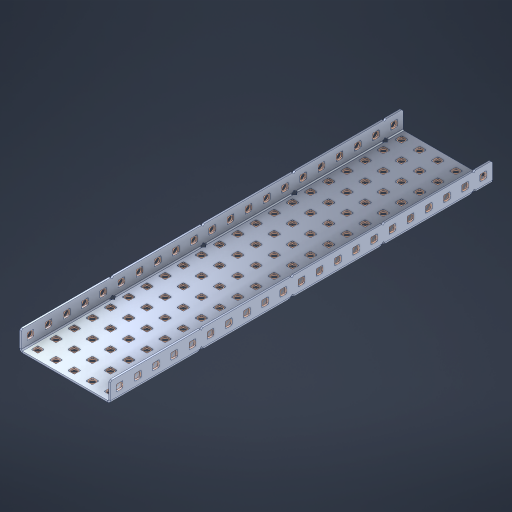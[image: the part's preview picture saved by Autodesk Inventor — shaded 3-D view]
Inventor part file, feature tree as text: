
AUTODESK INVENTOR PART (.ipt)
format: ipt  version: 2023 (Build 270158000, 158)  size: 1,724,416 bytes
history: native  units: in
note: dims shown in document units (in); Inventor stores cm internally (conversion verified against a paired STEP export)
features: other x152, extrude x146, sheet_metal_op x10, sketch x8, mirror x1, pattern_linear x1, chamfer x1
ambient origin geometry x8: Origin, YZ Plane, XZ Plane, XY Plane, X Axis, Y Axis, Z Axis, Center Point
bodies: Solid1 (feature_tree), Body (feature_tree)
feature tree (319):
  other  "Flange Pattern Plane"
  sheet_metal_op  "Flange Pattern"
  sheet_metal_op  "Body Pattern"
  other  "Arc Length"
  mirror  "Notch Mirror"
  pattern_linear  "Notch Pattern"  Spacing1=0.1875in  [1 undecoded]
  chamfer  "End Chamfer"
  extrude  "Half Cut"  Depth=0.0469in
  sketch  "Sketch1"  dims[d0=2.5in]
  other  "Plate1"
  sketch  "Sketch2"  dims[d1=10.5in]
  other  "Plate2"
  sheet_metal_op  "Bend1"
  sheet_metal_op  "Corner1"
  sketch  "Sketch3"  dims[d2=0.0469in]
  other  "Flange Pattern Sketch"
  sketch  "Sketch7"  dims[d3=0.0469in]
  other  "Srf1"
  other  "Srf2"
  sketch  "Sketch8"  dims[d4=0.0234in]
  sketch  "Sketch9"  dims[d5=0.0938in]
  other  "Srf91"
  sheet_metal_op  "Body Pattern Sketch"
  other  "Srf92"
  sketch  "Sketch13"  dims[d6=0.0469in]
  sketch  "Sketch14"  dims[d7=0.5in d8=90.0deg d9=0.0312in d10=0.1875in d11=0.0469in d12=0.0469in d16=0.182in d17=0.02in d18=0.0469in d19=0.0in d20=0.25in d21=0.25in d46=0.172in d47=1.0in d48=0.0in d49=0.182in d50=0.02in d51=0.25in d52=0.25in d53=0.0469in d54=0.0in d55=0.172in d56=1.0in d57=0.0in d60=8.2677in d62=0.5in d63=1.9685in d65=0.5in d85=0.1227in d86=0.1659in d88=0.04in d89=0.0469in d90=0.0in d91=0.04in d92=0.0491in d95=2.5in d96=0.04in d97=0.25in d98=45.0deg d101=0.0in d102=2.497in d131=2.5in d132=8.2677in d134=0.5in d139=0.5in]
  other  "Srf856"
  other  "Srf1310"
  other  "Srf1311"
  other  "Srf1312"
  other  "Srf1376"
  other  "Srf1377"
  other  "Srf1728"
  other  "Srf1755"
  other  "Srf1878"
  other  "Srf1879"
  other  "Srf1880"
  other  "Srf1881"
  other  "Srf1882"
  other  "Srf1883"
  other  "Srf1884"
  other  "Srf1885"
  other  "Srf1886"
  other  "Srf1887"
  other  "Srf1888"
  other  "Srf1889"
  other  "Srf1890"
  other  "Srf1891"
  other  "Srf1892"
  other  "Srf1893"
  other  "Srf1894"
  other  "Srf1895"
  other  "Srf1896"
  other  "Srf1897"
  other  "Srf1898"
  other  "Srf1899"
  other  "Srf1900"
  other  "Srf1901"
  other  "Srf1902"
  other  "Srf1903"
  other  "Srf1904"
  other  "Srf1905"
  other  "Srf1906"
  other  "Srf1942"
  other  "Srf1943"
  other  "Srf1944"
  other  "Srf1945"
  other  "Srf1946"
  other  "Srf1947"
  other  "Srf1948"
  other  "Srf1949"
  other  "Srf1950"
  other  "Srf1951"
  other  "Srf1952"
  other  "Srf1953"
  other  "Srf1954"
  other  "Srf1955"
  other  "Srf1956"
  other  "Srf1957"
  other  "Srf1958"
  other  "Srf1959"
  other  "Srf1960"
  other  "Srf1961"
  other  "Srf1962"
  other  "Srf1963"
  other  "Srf1964"
  other  "Srf1965"
  other  "Srf1966"
  other  "Srf1967"
  other  "Srf1968"
  other  "Srf1969"
  other  "Srf1970"
  other  "Srf2111"
  other  "Srf2112"
  other  "Srf2113"
  other  "Srf2114"
  other  "Srf2115"
  other  "Srf2116"
  other  "Srf2117"
  other  "Srf2146"
  other  "Srf2147"
  other  "Srf2148"
  other  "Srf2149"
  other  "Srf2150"
  other  "Srf2151"
  other  "Srf2152"
  other  "Srf2153"
  other  "Srf2154"
  other  "Srf2155"
  other  "Srf2156"
  other  "Srf2157"
  other  "Srf2158"
  other  "Srf2159"
  other  "Srf2160"
  other  "Srf2161"
  other  "Srf2162"
  other  "Srf2163"
  other  "Srf2164"
  other  "Srf2165"
  other  "Srf2166"
  other  "Srf2167"
  other  "Srf2168"
  other  "Srf2169"
  other  "Srf2170"
  other  "Srf2171"
  other  "Srf2172"
  other  "Srf2173"
  other  "Srf2174"
  other  "Srf2175"
  other  "Srf2176"
  other  "Srf2177"
  other  "Srf2178"
  other  "Srf2179"
  other  "Srf2180"
  other  "Srf2181"
  other  "Srf2182"
  other  "Srf2183"
  other  "Srf2184"
  other  "Srf2185"
  other  "Srf2186"
  other  "Srf2187"
  other  "Srf2188"
  other  "Srf2189"
  other  "Srf2190"
  other  "Srf2191"
  other  "Srf2192"
  other  "Srf2193"
  other  "Srf2194"
  other  "Srf2195"
  other  "Srf2196"
  other  "Srf2197"
  other  "Srf2198"
  other  "Srf2199"
  other  "Srf2200"
  other  "Srf2201"
  other  "Srf2202"
  other  "Srf2203"
  other  "Srf2204"
  other  "Srf2205"
  other  "Srf2206"
  other  "Srf2207"
  other  "Srf2208"
  other  "Srf2209"
  other  "Srf2210"
  other  "Srf2211"
  other  "Srf2212"
  other  "Srf2213"
  other  "Srf2214"
  other  "Srf2215"
  sheet_metal_op  "Flange Stamp"
  sheet_metal_op  "Flange Circle"
  sheet_metal_op  "Body Stamp"
  sheet_metal_op  "Body Circle"
  sheet_metal_op  "Notch"
  extrude  "ExtrusionSrf2"  Depth=0.0469in
  extrude  "ExtrusionSrf92"  Depth=2.5in
  extrude  "ExtrusionSrf856"  Depth=0.02in
  extrude  "ExtrusionSrf1310"  Depth=0.0469in
  extrude  "ExtrusionSrf1311"  TaperAngle=0.0deg  [1 undecoded]
  extrude  "ExtrusionSrf1312"  Depth=0.25in
  extrude  "ExtrusionSrf1376"  Depth=0.25in
  extrude  "ExtrusionSrf1377"  Depth=2.5in
  extrude  "ExtrusionSrf1728"  Depth=2.5in TaperAngle=0.0deg
  extrude  "ExtrusionSrf1755"  Depth=2.5in
  extrude  "ExtrusionSrf1878"  Depth=0.02in
  extrude  "ExtrusionSrf1879"  Depth=0.25in
  extrude  "ExtrusionSrf1880"  Depth=0.25in
  extrude  "ExtrusionSrf1881"  Depth=0.0469in
  extrude  "ExtrusionSrf1882"  TaperAngle=0.0deg  [1 undecoded]
  extrude  "ExtrusionSrf1883"  Depth=2.5in
  extrude  "ExtrusionSrf1884"  Depth=2.5in TaperAngle=0.0deg
  extrude  "ExtrusionSrf1885"  Depth=2.5in
  extrude  "ExtrusionSrf1886"  Depth=2.5in
  extrude  "ExtrusionSrf1887"  Depth=2.5in
  extrude  "ExtrusionSrf1888"  Depth=2.5in
  extrude  "ExtrusionSrf1889"  Depth=2.5in
  extrude  "ExtrusionSrf1890"  Depth=0.0469in
  extrude  "ExtrusionSrf1891"  TaperAngle=0.0deg  [1 undecoded]
  extrude  "ExtrusionSrf1892"  Depth=2.5in
  extrude  "ExtrusionSrf1893"  Depth=2.5in
  extrude  "ExtrusionSrf1894"  Depth=2.5in
  extrude  "ExtrusionSrf1895"  Depth=0.25in TaperAngle=45.0deg
  extrude  "ExtrusionSrf1896"  TaperAngle=0.0deg  [1 undecoded]
  extrude  "ExtrusionSrf1897"  Depth=2.5in
  extrude  "ExtrusionSrf1898"  Depth=2.5in
  extrude  "ExtrusionSrf1899"  Depth=2.5in
  extrude  "ExtrusionSrf1900"  Depth=2.5in
  extrude  "ExtrusionSrf1901"  Depth=2.5in
  extrude  "ExtrusionSrf1902"  [1 undecoded]
  extrude  "ExtrusionSrf1903"  [1 undecoded]
  extrude  "ExtrusionSrf1904"  [1 undecoded]
  extrude  "ExtrusionSrf1905"  [1 undecoded]
  extrude  "ExtrusionSrf1906"  [1 undecoded]
  extrude  "ExtrusionSrf1942"  [1 undecoded]
  extrude  "ExtrusionSrf1943"  [1 undecoded]
  extrude  "ExtrusionSrf1944"  [1 undecoded]
  extrude  "ExtrusionSrf1945"  [1 undecoded]
  extrude  "ExtrusionSrf1946"  [1 undecoded]
  extrude  "ExtrusionSrf1947"  [1 undecoded]
  extrude  "ExtrusionSrf1948"  [1 undecoded]
  extrude  "ExtrusionSrf1949"  [1 undecoded]
  extrude  "ExtrusionSrf1950"  [1 undecoded]
  extrude  "ExtrusionSrf1951"  [1 undecoded]
  extrude  "ExtrusionSrf1952"  [1 undecoded]
  extrude  "ExtrusionSrf1953"  [1 undecoded]
  extrude  "ExtrusionSrf1954"  [1 undecoded]
  extrude  "ExtrusionSrf1955"  [1 undecoded]
  extrude  "ExtrusionSrf1956"  [1 undecoded]
  extrude  "ExtrusionSrf1957"  [1 undecoded]
  extrude  "ExtrusionSrf1958"  [1 undecoded]
  extrude  "ExtrusionSrf1959"  [1 undecoded]
  extrude  "ExtrusionSrf1960"  [1 undecoded]
  extrude  "ExtrusionSrf1961"  [1 undecoded]
  extrude  "ExtrusionSrf1962"  [1 undecoded]
  extrude  "ExtrusionSrf1963"  [1 undecoded]
  extrude  "ExtrusionSrf1964"  [1 undecoded]
  extrude  "ExtrusionSrf1965"  [1 undecoded]
  extrude  "ExtrusionSrf1966"  [1 undecoded]
  extrude  "ExtrusionSrf1967"  [1 undecoded]
  extrude  "ExtrusionSrf1968"  [1 undecoded]
  extrude  "ExtrusionSrf1969"  [1 undecoded]
  extrude  "ExtrusionSrf1970"  [1 undecoded]
  extrude  "ExtrusionSrf2111"  [1 undecoded]
  extrude  "ExtrusionSrf2112"  [1 undecoded]
  extrude  "ExtrusionSrf2113"  [1 undecoded]
  extrude  "ExtrusionSrf2114"  [1 undecoded]
  extrude  "ExtrusionSrf2115"  [1 undecoded]
  extrude  "ExtrusionSrf2116"  [1 undecoded]
  extrude  "ExtrusionSrf2117"  [1 undecoded]
  extrude  "ExtrusionSrf2146"  [1 undecoded]
  extrude  "ExtrusionSrf2147"  [1 undecoded]
  extrude  "ExtrusionSrf2148"  [1 undecoded]
  extrude  "ExtrusionSrf2149"  [1 undecoded]
  extrude  "ExtrusionSrf2150"  [1 undecoded]
  extrude  "ExtrusionSrf2151"  [1 undecoded]
  extrude  "ExtrusionSrf2152"  [1 undecoded]
  extrude  "ExtrusionSrf2153"  [1 undecoded]
  extrude  "ExtrusionSrf2154"  [1 undecoded]
  extrude  "ExtrusionSrf2155"  [1 undecoded]
  extrude  "ExtrusionSrf2156"  [1 undecoded]
  extrude  "ExtrusionSrf2157"  [1 undecoded]
  extrude  "ExtrusionSrf2158"  [1 undecoded]
  extrude  "ExtrusionSrf2159"  [1 undecoded]
  extrude  "ExtrusionSrf2160"  [1 undecoded]
  extrude  "ExtrusionSrf2161"  [1 undecoded]
  extrude  "ExtrusionSrf2162"  [1 undecoded]
  extrude  "ExtrusionSrf2163"  [1 undecoded]
  extrude  "ExtrusionSrf2164"  [1 undecoded]
  extrude  "ExtrusionSrf2165"  [1 undecoded]
  extrude  "ExtrusionSrf2166"  [1 undecoded]
  extrude  "ExtrusionSrf2167"  [1 undecoded]
  extrude  "ExtrusionSrf2168"  [1 undecoded]
  extrude  "ExtrusionSrf2169"  [1 undecoded]
  extrude  "ExtrusionSrf2170"  [1 undecoded]
  extrude  "ExtrusionSrf2171"  [1 undecoded]
  extrude  "ExtrusionSrf2172"  [1 undecoded]
  extrude  "ExtrusionSrf2173"  [1 undecoded]
  extrude  "ExtrusionSrf2174"  [1 undecoded]
  extrude  "ExtrusionSrf2175"  [1 undecoded]
  extrude  "ExtrusionSrf2176"  [1 undecoded]
  extrude  "ExtrusionSrf2177"  [1 undecoded]
  extrude  "ExtrusionSrf2178"  [1 undecoded]
  extrude  "ExtrusionSrf2179"  [1 undecoded]
  extrude  "ExtrusionSrf2180"  [1 undecoded]
  extrude  "ExtrusionSrf2181"  [1 undecoded]
  extrude  "ExtrusionSrf2182"  [1 undecoded]
  extrude  "ExtrusionSrf2183"  [1 undecoded]
  extrude  "ExtrusionSrf2184"  [1 undecoded]
  extrude  "ExtrusionSrf2185"  [1 undecoded]
  extrude  "ExtrusionSrf2186"  [1 undecoded]
  extrude  "ExtrusionSrf2187"  [1 undecoded]
  extrude  "ExtrusionSrf2188"  [1 undecoded]
  extrude  "ExtrusionSrf2189"  [1 undecoded]
  extrude  "ExtrusionSrf2190"  [1 undecoded]
  extrude  "ExtrusionSrf2191"  [1 undecoded]
  extrude  "ExtrusionSrf2192"  [1 undecoded]
  extrude  "ExtrusionSrf2193"  [1 undecoded]
  extrude  "ExtrusionSrf2194"  [1 undecoded]
  extrude  "ExtrusionSrf2195"  [1 undecoded]
  extrude  "ExtrusionSrf2196"  [1 undecoded]
  extrude  "ExtrusionSrf2197"  [1 undecoded]
  extrude  "ExtrusionSrf2198"  [1 undecoded]
  extrude  "ExtrusionSrf2199"  [1 undecoded]
  extrude  "ExtrusionSrf2200"  [1 undecoded]
  extrude  "ExtrusionSrf2201"  [1 undecoded]
  extrude  "ExtrusionSrf2202"  [1 undecoded]
  extrude  "ExtrusionSrf2203"  [1 undecoded]
  extrude  "ExtrusionSrf2204"  [1 undecoded]
  extrude  "ExtrusionSrf2205"  [1 undecoded]
  extrude  "ExtrusionSrf2206"  [1 undecoded]
  extrude  "ExtrusionSrf2207"  [1 undecoded]
  extrude  "ExtrusionSrf2208"  [1 undecoded]
  extrude  "ExtrusionSrf2209"  [1 undecoded]
  extrude  "ExtrusionSrf2210"  [1 undecoded]
  extrude  "ExtrusionSrf2211"  [1 undecoded]
  extrude  "ExtrusionSrf2212"  [1 undecoded]
  extrude  "ExtrusionSrf2213"  [1 undecoded]
  extrude  "ExtrusionSrf2214"  [1 undecoded]
  extrude  "ExtrusionSrf2215"  [1 undecoded]
note: 116 required parameter values undecoded (feature->parameter linkage not recoverable at this tier; creation-order binding heuristic only, values carry confidence <= 0.55)
